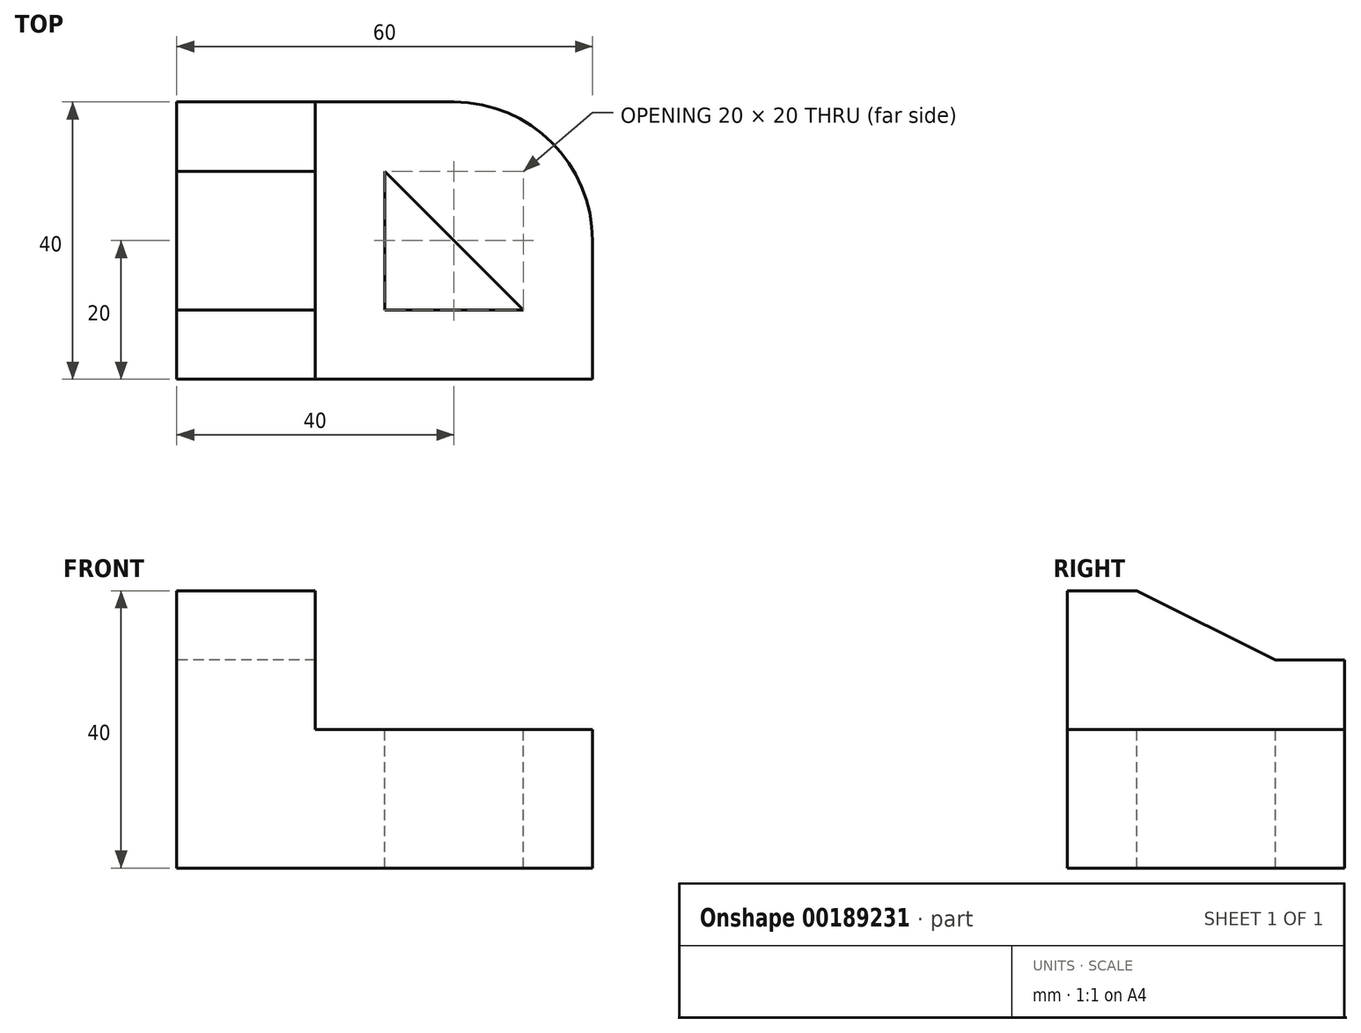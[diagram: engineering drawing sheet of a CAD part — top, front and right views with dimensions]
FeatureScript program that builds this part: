
annotation { "Feature Type Name" : "Feature", "Feature Type Description" : "" }
export const myFeature = defineFeature(function(context is Context, id is Id, definition is map)
    precondition{}
    {
        {
            var Q0;
            Q0=qCreatedBy(makeId("Top.planeOp"),FACE);
            var sketch = newSketch(context, id + "F0", { "sketchPlane" : qUnion([Q0])});
            skLineSegment(sketch, "E0.bottom", {"start": v(0, 0) * mm, "end": v(60, 0) * mm});
            skLineSegment(sketch, "E0.top", {"start": v(0, 40) * mm, "end": v(40, 40) * mm});
            skLineSegment(sketch, "E0.left", {"start": v(0, 0) * mm, "end": v(0, 40) * mm});
            skLineSegment(sketch, "E0.right", {"start": v(60, 0) * mm, "end": v(60, 20) * mm});
            skPoint(sketch, "E1.visualSharp", {"position": v(60, 40) * mm});
            skArc(sketch, "E1.filletArc", {"start": v(60, 20) * mm, "mid": v(54.14, 34.14) * mm, "end": v(40, 40) * mm});
            skSolve(sketch);
        }
        {
            var Q0;
            Q0=makeQuery(id+"F0.imprint","IMPRINT",FACE,{"disambiguationData":[TD([[makeQuery(id+"F0.imprint","IMPRINT",EDGE,{"derivedFrom":sQuery(id+"F0.wireOp",EDGE,"E0.bottom")}),1.0]])]});
            extrude(context, id + "F1", {"entities" : qUnion([Q0]), "depth" : 20 * mm});
        }
        {
            var Q0;
            Q0=makeQuery(id+"F1.opExtrude","CAP_FACE",FACE,{"disambiguationData":[OSD([sQuery(id+"F0.wireOp",EDGE,"E0.bottom"),sQuery(id+"F0.wireOp",EDGE,"E0.top"),sQuery(id+"F0.wireOp",EDGE,"E0.left"),sQuery(id+"F0.wireOp",EDGE,"E0.right"),sQuery(id+"F0.wireOp",EDGE,"E1.filletArc")])],"isStart":false});
            var sketch = newSketch(context, id + "F2", { "sketchPlane" : qUnion([Q0])});
            skLineSegment(sketch, "E2", {"start": v(30, 30) * mm, "end": v(30, 10) * mm});
            skLineSegment(sketch, "E3", {"start": v(30, 10) * mm, "end": v(50, 10) * mm});
            skLineSegment(sketch, "E4", {"start": v(50, 10) * mm, "end": v(30, 30) * mm});
            skSolve(sketch);
        }
        {
            var Q0;
            Q0=makeQuery(id+"F2.imprint","IMPRINT",FACE,{"disambiguationData":[TD([[makeQuery(id+"F2.imprint","IMPRINT",EDGE,{"derivedFrom":sQuery(id+"F2.wireOp",EDGE,"E2")}),1.0]])]});
            extrude(context, id + "F3", {"entities" : qUnion([Q0]), "operationType" : NewBodyOperationType.REMOVE, "endBound" : BoundingType.THROUGH_ALL, "oppositeDirection" : true, "depth" : 25 * mm});
        }
        {
            var Q0;
            Q0=qCreatedBy(makeId("Right.planeOp"),FACE);
            var sketch = newSketch(context, id + "F4", { "sketchPlane" : qUnion([Q0])});
            skLineSegment(sketch, "E5.0", {"start": v(0, 20) * mm, "end": v(40, 20) * mm});
            skLineSegment(sketch, "E6", {"start": v(0, 20) * mm, "end": v(0, 40) * mm});
            skLineSegment(sketch, "E7", {"start": v(0, 40) * mm, "end": v(10, 40) * mm});
            skLineSegment(sketch, "E8", {"start": v(10, 40) * mm, "end": v(30, 30) * mm});
            skLineSegment(sketch, "E9", {"start": v(30, 30) * mm, "end": v(40, 30) * mm});
            skLineSegment(sketch, "E10", {"start": v(40, 30) * mm, "end": v(40, 20) * mm});
            skSolve(sketch);
        }
        {
            var Q0;
            Q0=makeQuery(id+"F4.imprint","IMPRINT",FACE,{"disambiguationData":[TD([[makeQuery(id+"F4.imprint","IMPRINT",EDGE,{"derivedFrom":sQuery(id+"F4.wireOp",EDGE,"E5.0")}),1.0]])]});
            extrude(context, id + "F5", {"entities" : qUnion([Q0]), "operationType" : NewBodyOperationType.ADD, "depth" : 20 * mm});
        }
    });
